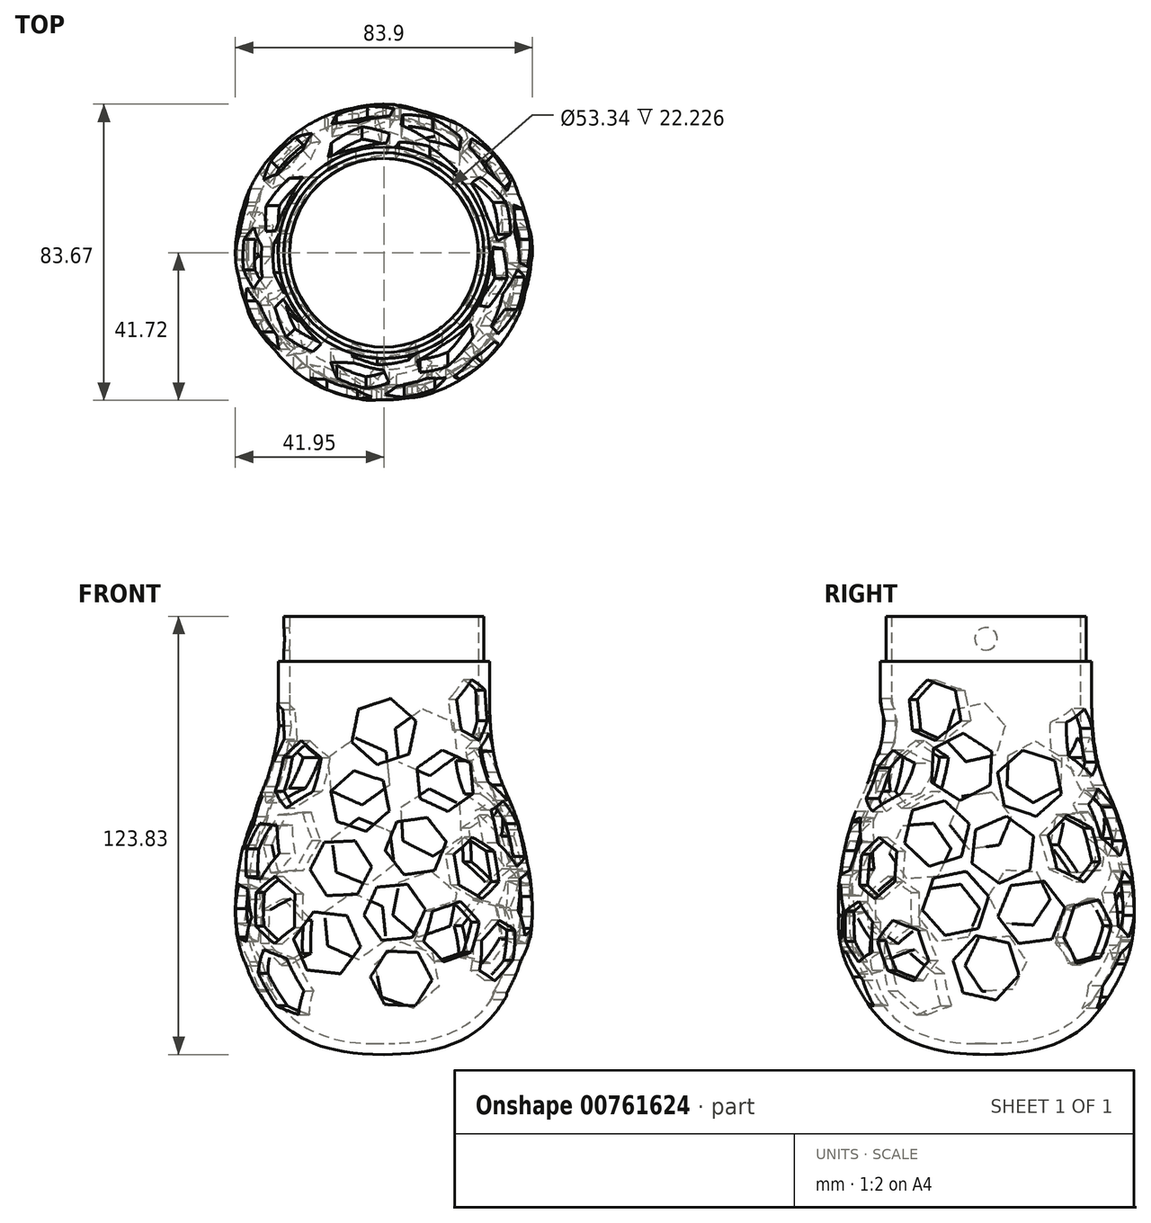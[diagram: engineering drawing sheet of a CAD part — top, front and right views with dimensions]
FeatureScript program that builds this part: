
annotation { "Feature Type Name" : "Feature", "Feature Type Description" : "" }
export const myFeature = defineFeature(function(context is Context, id is Id, definition is map)
    precondition{}
    {
        {
            var Q0;
            Q0=qCreatedBy(makeId("Front.planeOp"),FACE);
            var sketch = newSketch(context, id + "F0", { "sketchPlane" : qUnion([Q0])});
            skLineSegment(sketch, "E0.left", {"start": v(-29.85, -28.58) * mm, "end": v(-29.85, -50.8) * mm});
            skLineSegment(sketch, "E1", {"start": v(0, -149.22) * mm, "end": v(0, -152.4) * mm});
            skFitSpline(sketch, "E2", {"points": [v(-29.85, -50.8) * mm, v(-36.24, -82.2) * mm, v(-41.22, -101.6) * mm, v(-40.98, -121.67) * mm, v(-34.22, -136.68) * mm, v(0, -152.4) * mm], "startDerivative": vector(-0.05, -263.37) * mm, "endDerivative": vector(273.36, 0) * mm});
            skPoint(sketch, "E3.orphan", {"position": v(0, 0) * mm});
            skFitSpline(sketch, "E4.0", {"points": [v(-26.67, -50.8) * mm, v(-26.67, -56.4) * mm, v(-27.08, -63.07) * mm, v(-28.2, -69.67) * mm, v(-29.29, -73.73) * mm, v(-30.52, -77.1) * mm, v(-31.58, -79.5) * mm, v(-32.39, -81.3) * mm, v(-32.97, -82.6) * mm, v(-33.52, -83.93) * mm, v(-34.05, -85.32) * mm, v(-34.57, -86.78) * mm, v(-35.23, -88.8) * mm, v(-36, -91.47) * mm, v(-36.8, -94.82) * mm, v(-37.5, -98.27) * mm, v(-38.06, -101.77) * mm, v(-38.61, -106.45) * mm, v(-38.84, -111.04) * mm, v(-38.68, -115.4) * mm, v(-38.41, -118) * mm, v(-38.09, -120) * mm, v(-37.69, -121.9) * mm, v(-37.05, -124.18) * mm, v(-36.06, -126.82) * mm, v(-35.05, -128.98) * mm, v(-34.12, -130.72) * mm, v(-33.38, -132.03) * mm, v(-32.58, -133.36) * mm, v(-31.86, -134.5) * mm, v(-31.27, -135.4) * mm, v(-30.66, -136.31) * mm, v(-29.88, -137.43) * mm, v(-28.89, -138.73) * mm, v(-27.46, -140.42) * mm, v(-25.43, -142.4) * mm, v(-22.42, -144.57) * mm, v(-18.61, -146.45) * mm, v(-12.18, -148.46) * mm, v(-5.5, -149.23) * mm, v(0, -149.23) * mm]});
            skLineSegment(sketch, "E4.1", {"start": v(-26.67, -28.58) * mm, "end": v(-26.67, -50.8) * mm});
            skLineSegment(sketch, "E5", {"start": v(-26.67, 0) * mm, "end": v(0, 0) * mm, "construction": true});
            skLineSegment(sketch, "E6", {"start": v(0, -149.22) * mm, "end": v(0, 0) * mm, "construction": true});
            skLineSegment(sketch, "E7", {"start": v(-26.67, -28.58) * mm, "end": v(-29.85, -28.58) * mm});
            skLineSegment(sketch, "E8", {"start": v(-26.67, -28.58) * mm, "end": v(-26.67, 0) * mm, "construction": true});
            skSolve(sketch);
        }
        {
            var Q0;
            Q0 = qSketchRegion(id + "F0", true);
            var Q1;
            Q1=sQuery(id+"F0.wireOp",EDGE,"E6");
            revolve(context, id + "F1", {"surfaceOperationType" : NewSurfaceOperationType.NEW, "entities" : qUnion([Q0]), "axis" : qUnion([Q1]), "revolveType" : RevolveType.FULL});
        }
        {
            var Q0;
            Q0=qCreatedBy(makeId("Right.planeOp"),FACE);
            var sketch = newSketch(context, id + "F2", { "sketchPlane" : qUnion([Q0])});
            skCircle(sketch, "E9.cCircle", {"center": v(-18.57, -94.91) * mm, "radius": 7.55 * mm, "construction": true});
            skLineSegment(sketch, "E9.0", {"start": v(-22.35, -102.76) * mm, "end": v(-27.26, -95.57) * mm});
            skLineSegment(sketch, "E9.1", {"start": v(-27.26, -95.57) * mm, "end": v(-23.48, -87.72) * mm});
            skLineSegment(sketch, "E9.2", {"start": v(-23.48, -87.72) * mm, "end": v(-14.8, -87.06) * mm});
            skLineSegment(sketch, "E9.3", {"start": v(-14.8, -87.06) * mm, "end": v(-9.89, -94.26) * mm});
            skLineSegment(sketch, "E9.4", {"start": v(-9.89, -94.26) * mm, "end": v(-13.66, -102.11) * mm});
            skLineSegment(sketch, "E9.5", {"start": v(-13.66, -102.11) * mm, "end": v(-22.35, -102.76) * mm});
            skCircle(sketch, "E10.cCircle", {"center": v(-10.38, -112.38) * mm, "radius": 7.55 * mm, "construction": true});
            skLineSegment(sketch, "E10.0", {"start": v(-13.65, -120.45) * mm, "end": v(-19.01, -113.59) * mm});
            skLineSegment(sketch, "E10.1", {"start": v(-19.01, -113.59) * mm, "end": v(-15.74, -105.51) * mm});
            skLineSegment(sketch, "E10.2", {"start": v(-15.74, -105.51) * mm, "end": v(-7.12, -104.3) * mm});
            skLineSegment(sketch, "E10.3", {"start": v(-7.12, -104.3) * mm, "end": v(-1.76, -111.17) * mm});
            skLineSegment(sketch, "E10.4", {"start": v(-1.76, -111.17) * mm, "end": v(-5.02, -119.25) * mm});
            skLineSegment(sketch, "E10.5", {"start": v(-5.02, -119.25) * mm, "end": v(-13.65, -120.45) * mm});
            skPoint(sketch, "E10.0.midPoint", {"position": v(-16.33, -117.02) * mm});
            skCircle(sketch, "E11.cCircle", {"center": v(-1.56, -86.32) * mm, "radius": 7.55 * mm, "construction": true});
            skLineSegment(sketch, "E11.0", {"start": v(-4.8, -94.4) * mm, "end": v(-10.19, -87.55) * mm});
            skLineSegment(sketch, "E11.1", {"start": v(-10.19, -87.55) * mm, "end": v(-6.94, -79.46) * mm});
            skLineSegment(sketch, "E11.2", {"start": v(-6.94, -79.46) * mm, "end": v(1.69, -78.24) * mm});
            skLineSegment(sketch, "E11.3", {"start": v(1.69, -78.24) * mm, "end": v(7.07, -85.1) * mm});
            skLineSegment(sketch, "E11.4", {"start": v(7.07, -85.1) * mm, "end": v(3.82, -93.18) * mm});
            skLineSegment(sketch, "E11.5", {"start": v(3.82, -93.18) * mm, "end": v(-4.8, -94.4) * mm});
            skPoint(sketch, "E11.0.midPoint", {"position": v(-7.5, -90.98) * mm});
            skCircle(sketch, "E12.cCircle", {"center": v(9.45, -108.03) * mm, "radius": 7.55 * mm, "construction": true});
            skLineSegment(sketch, "E12.0", {"start": v(4.64, -115.3) * mm, "end": v(0.76, -107.5) * mm});
            skLineSegment(sketch, "E12.1", {"start": v(0.76, -107.5) * mm, "end": v(5.57, -100.23) * mm});
            skLineSegment(sketch, "E12.2", {"start": v(5.57, -100.23) * mm, "end": v(14.26, -100.77) * mm});
            skLineSegment(sketch, "E12.3", {"start": v(14.26, -100.77) * mm, "end": v(18.15, -108.57) * mm});
            skLineSegment(sketch, "E12.4", {"start": v(18.15, -108.57) * mm, "end": v(13.34, -115.83) * mm});
            skLineSegment(sketch, "E12.5", {"start": v(13.34, -115.83) * mm, "end": v(4.64, -115.3) * mm});
            skPoint(sketch, "E12.0.midPoint", {"position": v(2.7, -111.4) * mm});
            skCircle(sketch, "E13.cCircle", {"center": v(13.67, -72.51) * mm, "radius": 7.55 * mm, "construction": true});
            skLineSegment(sketch, "E13.0", {"start": v(13.34, -81.22) * mm, "end": v(5.97, -76.58) * mm});
            skLineSegment(sketch, "E13.1", {"start": v(5.97, -76.58) * mm, "end": v(6.3, -67.88) * mm});
            skLineSegment(sketch, "E13.2", {"start": v(6.3, -67.88) * mm, "end": v(14, -63.8) * mm});
            skLineSegment(sketch, "E13.3", {"start": v(14, -63.8) * mm, "end": v(21.37, -68.44) * mm});
            skLineSegment(sketch, "E13.4", {"start": v(21.37, -68.44) * mm, "end": v(21.04, -77.15) * mm});
            skLineSegment(sketch, "E13.5", {"start": v(21.04, -77.15) * mm, "end": v(13.34, -81.22) * mm});
            skPoint(sketch, "E13.0.midPoint", {"position": v(9.65, -78.9) * mm});
            skCircle(sketch, "E14.cCircle", {"center": v(-3.06, -61.34) * mm, "radius": 7.55 * mm, "construction": true});
            skLineSegment(sketch, "E14.0", {"start": v(-5.67, -69.66) * mm, "end": v(-11.56, -63.24) * mm});
            skLineSegment(sketch, "E14.1", {"start": v(-11.56, -63.24) * mm, "end": v(-8.96, -54.93) * mm});
            skLineSegment(sketch, "E14.2", {"start": v(-8.96, -54.93) * mm, "end": v(-0.45, -53.03) * mm});
            skLineSegment(sketch, "E14.3", {"start": v(-0.45, -53.03) * mm, "end": v(5.44, -59.44) * mm});
            skLineSegment(sketch, "E14.4", {"start": v(5.44, -59.44) * mm, "end": v(2.84, -67.76) * mm});
            skLineSegment(sketch, "E14.5", {"start": v(2.84, -67.76) * mm, "end": v(-5.67, -69.66) * mm});
            skPoint(sketch, "E14.0.midPoint", {"position": v(-8.61, -66.45) * mm});
            skCircle(sketch, "E15.cCircle", {"center": v(2.78, -126.74) * mm, "radius": 7.55 * mm, "construction": true});
            skLineSegment(sketch, "E15.0", {"start": v(-1.06, -134.56) * mm, "end": v(-5.91, -127.32) * mm});
            skLineSegment(sketch, "E15.1", {"start": v(-5.91, -127.32) * mm, "end": v(-2.07, -119.5) * mm});
            skLineSegment(sketch, "E15.2", {"start": v(-2.07, -119.5) * mm, "end": v(6.62, -118.92) * mm});
            skLineSegment(sketch, "E15.3", {"start": v(6.62, -118.92) * mm, "end": v(11.47, -126.15) * mm});
            skLineSegment(sketch, "E15.4", {"start": v(11.47, -126.15) * mm, "end": v(7.63, -133.97) * mm});
            skLineSegment(sketch, "E15.5", {"start": v(7.63, -133.97) * mm, "end": v(-1.06, -134.56) * mm});
            skPoint(sketch, "E15.0.midPoint", {"position": v(-3.48, -130.94) * mm});
            skSolve(sketch);
        }
        {
            var Q0;
            Q0 = qSketchRegion(id + "F2", true);
            var Q1;
            Q1=makeQuery(id+"F1.opRevolve","SWEPT_FACE",FACE,{"disambiguationData":[OSD([sQuery(id+"F0.wireOp",EDGE,"E4.0")])]});
            extrude(context, id + "F3", {"entities" : qUnion([Q0]), "operationType" : NewBodyOperationType.REMOVE, "endBound" : BoundingType.THROUGH_ALL, "oppositeDirection" : true, "depth" : 25.4 * mm, "endBoundEntityFace" : qUnion([Q1]), "offsetDistance" : 25.4 * mm});
        }
        {
            var Q0;
            Q0=qCreatedBy(makeId("Front.planeOp"),FACE);
            var sketch = newSketch(context, id + "F4", { "sketchPlane" : qUnion([Q0])});
            skCircle(sketch, "E16.cCircle", {"center": v(-7.1, -72.4) * mm, "radius": 8.26 * mm, "construction": true});
            skLineSegment(sketch, "E16.0", {"start": v(-8.02, -62.9) * mm, "end": v(0.66, -66.85) * mm});
            skLineSegment(sketch, "E16.1", {"start": v(0.66, -66.85) * mm, "end": v(1.58, -76.34) * mm});
            skLineSegment(sketch, "E16.2", {"start": v(1.58, -76.34) * mm, "end": v(-6.18, -81.88) * mm});
            skLineSegment(sketch, "E16.3", {"start": v(-6.18, -81.88) * mm, "end": v(-14.86, -77.94) * mm});
            skLineSegment(sketch, "E16.4", {"start": v(-14.86, -77.94) * mm, "end": v(-15.78, -68.45) * mm});
            skLineSegment(sketch, "E16.5", {"start": v(-15.78, -68.45) * mm, "end": v(-8.02, -62.9) * mm});
            skPoint(sketch, "E16.0.midPoint", {"position": v(-3.68, -64.88) * mm});
            skCircle(sketch, "E17.cCircle", {"center": v(11.95, -64.17) * mm, "radius": 8.26 * mm, "construction": true});
            skLineSegment(sketch, "E17.0", {"start": v(10.94, -54.7) * mm, "end": v(19.66, -58.56) * mm});
            skLineSegment(sketch, "E17.1", {"start": v(19.66, -58.56) * mm, "end": v(20.67, -68.04) * mm});
            skLineSegment(sketch, "E17.2", {"start": v(20.67, -68.04) * mm, "end": v(12.96, -73.65) * mm});
            skLineSegment(sketch, "E17.3", {"start": v(12.96, -73.65) * mm, "end": v(4.25, -69.79) * mm});
            skLineSegment(sketch, "E17.4", {"start": v(4.25, -69.79) * mm, "end": v(3.24, -60.3) * mm});
            skLineSegment(sketch, "E17.5", {"start": v(3.24, -60.3) * mm, "end": v(10.94, -54.7) * mm});
            skPoint(sketch, "E17.0.midPoint", {"position": v(15.3, -56.63) * mm});
            skCircle(sketch, "E18.cCircle", {"center": v(-5.9, -95.06) * mm, "radius": 8.26 * mm, "construction": true});
            skLineSegment(sketch, "E18.0", {"start": v(-7.14, -85.6) * mm, "end": v(1.67, -89.25) * mm});
            skLineSegment(sketch, "E18.1", {"start": v(1.67, -89.25) * mm, "end": v(2.91, -98.7) * mm});
            skLineSegment(sketch, "E18.2", {"start": v(2.91, -98.7) * mm, "end": v(-4.65, -104.5) * mm});
            skLineSegment(sketch, "E18.3", {"start": v(-4.65, -104.5) * mm, "end": v(-13.46, -100.86) * mm});
            skLineSegment(sketch, "E18.4", {"start": v(-13.46, -100.86) * mm, "end": v(-14.7, -91.4) * mm});
            skLineSegment(sketch, "E18.5", {"start": v(-14.7, -91.4) * mm, "end": v(-7.14, -85.6) * mm});
            skPoint(sketch, "E18.0.midPoint", {"position": v(-2.74, -87.43) * mm});
            skCircle(sketch, "E19.cCircle", {"center": v(-8.1, -116.11) * mm, "radius": 8.26 * mm, "construction": true});
            skLineSegment(sketch, "E19.0", {"start": v(-9.02, -106.62) * mm, "end": v(-0.34, -110.57) * mm});
            skLineSegment(sketch, "E19.1", {"start": v(-0.34, -110.57) * mm, "end": v(0.57, -120.06) * mm});
            skLineSegment(sketch, "E19.2", {"start": v(0.57, -120.06) * mm, "end": v(-7.19, -125.6) * mm});
            skLineSegment(sketch, "E19.3", {"start": v(-7.19, -125.6) * mm, "end": v(-15.86, -121.65) * mm});
            skLineSegment(sketch, "E19.4", {"start": v(-15.86, -121.65) * mm, "end": v(-16.78, -112.16) * mm});
            skLineSegment(sketch, "E19.5", {"start": v(-16.78, -112.16) * mm, "end": v(-9.02, -106.62) * mm});
            skPoint(sketch, "E19.0.midPoint", {"position": v(-4.68, -108.6) * mm});
            skCircle(sketch, "E20.cCircle", {"center": v(11.55, -109.9) * mm, "radius": 8.26 * mm, "construction": true});
            skLineSegment(sketch, "E20.0", {"start": v(13.32, -100.53) * mm, "end": v(20.55, -106.75) * mm});
            skLineSegment(sketch, "E20.1", {"start": v(20.55, -106.75) * mm, "end": v(18.78, -116.11) * mm});
            skLineSegment(sketch, "E20.2", {"start": v(18.78, -116.11) * mm, "end": v(9.78, -119.26) * mm});
            skLineSegment(sketch, "E20.3", {"start": v(9.78, -119.26) * mm, "end": v(2.55, -113.04) * mm});
            skLineSegment(sketch, "E20.4", {"start": v(2.55, -113.04) * mm, "end": v(4.33, -103.68) * mm});
            skLineSegment(sketch, "E20.5", {"start": v(4.33, -103.68) * mm, "end": v(13.32, -100.53) * mm});
            skPoint(sketch, "E20.0.midPoint", {"position": v(16.93, -103.64) * mm});
            skCircle(sketch, "E21.cCircle", {"center": v(13.36, -86.83) * mm, "radius": 8.26 * mm, "construction": true});
            skLineSegment(sketch, "E21.0", {"start": v(12.86, -77.31) * mm, "end": v(21.35, -81.65) * mm});
            skLineSegment(sketch, "E21.1", {"start": v(21.35, -81.65) * mm, "end": v(21.85, -91.17) * mm});
            skLineSegment(sketch, "E21.2", {"start": v(21.85, -91.17) * mm, "end": v(13.85, -96.35) * mm});
            skLineSegment(sketch, "E21.3", {"start": v(13.85, -96.35) * mm, "end": v(5.36, -92.02) * mm});
            skLineSegment(sketch, "E21.4", {"start": v(5.36, -92.02) * mm, "end": v(4.87, -82.5) * mm});
            skLineSegment(sketch, "E21.5", {"start": v(4.87, -82.5) * mm, "end": v(12.86, -77.31) * mm});
            skPoint(sketch, "E21.0.midPoint", {"position": v(17.1, -79.48) * mm});
            skCircle(sketch, "E22.cCircle", {"center": v(6.54, -129.95) * mm, "radius": 8.26 * mm, "construction": true});
            skLineSegment(sketch, "E22.0", {"start": v(4.73, -120.6) * mm, "end": v(13.74, -123.7) * mm});
            skLineSegment(sketch, "E22.1", {"start": v(13.74, -123.7) * mm, "end": v(15.55, -133.06) * mm});
            skLineSegment(sketch, "E22.2", {"start": v(15.55, -133.06) * mm, "end": v(8.34, -139.3) * mm});
            skLineSegment(sketch, "E22.3", {"start": v(8.34, -139.3) * mm, "end": v(-0.66, -136.2) * mm});
            skLineSegment(sketch, "E22.4", {"start": v(-0.66, -136.2) * mm, "end": v(-2.47, -126.83) * mm});
            skLineSegment(sketch, "E22.5", {"start": v(-2.47, -126.83) * mm, "end": v(4.73, -120.6) * mm});
            skPoint(sketch, "E22.0.midPoint", {"position": v(9.24, -122.15) * mm});
            skSolve(sketch);
        }
        {
            var Q0;
            Q0 = qSketchRegion(id + "F4", true);
            extrude(context, id + "F5", {"entities" : qUnion([Q0]), "operationType" : NewBodyOperationType.REMOVE, "endBound" : BoundingType.THROUGH_ALL, "oppositeDirection" : true, "depth" : 25.4 * mm, "offsetDistance" : 25.4 * mm});
        }
        {
            var Q0;
            Q0=qCreatedBy(makeId("Front.planeOp"),FACE);
            var sketch = newSketch(context, id + "F6", { "sketchPlane" : qUnion([Q0])});
            skCircle(sketch, "E23.cCircle", {"center": v(-12.14, -99.77) * mm, "radius": 7.55 * mm, "construction": true});
            skLineSegment(sketch, "E23.0", {"start": v(-16.14, -107.51) * mm, "end": v(-20.84, -100.18) * mm});
            skLineSegment(sketch, "E23.1", {"start": v(-20.84, -100.18) * mm, "end": v(-16.84, -92.44) * mm});
            skLineSegment(sketch, "E23.2", {"start": v(-16.84, -92.44) * mm, "end": v(-8.14, -92.03) * mm});
            skLineSegment(sketch, "E23.3", {"start": v(-8.14, -92.03) * mm, "end": v(-3.44, -99.37) * mm});
            skLineSegment(sketch, "E23.4", {"start": v(-3.44, -99.37) * mm, "end": v(-7.44, -107.1) * mm});
            skLineSegment(sketch, "E23.5", {"start": v(-7.44, -107.1) * mm, "end": v(-16.14, -107.51) * mm});
            skPoint(sketch, "E23.0.midPoint", {"position": v(-18.5, -103.84) * mm});
            skCircle(sketch, "E24.cCircle", {"center": v(3.05, -112.22) * mm, "radius": 7.55 * mm, "construction": true});
            skLineSegment(sketch, "E24.0", {"start": v(-0.59, -120.14) * mm, "end": v(-5.63, -113.03) * mm});
            skLineSegment(sketch, "E24.1", {"start": v(-5.63, -113.03) * mm, "end": v(-2, -105.11) * mm});
            skLineSegment(sketch, "E24.2", {"start": v(-2, -105.11) * mm, "end": v(6.68, -104.3) * mm});
            skLineSegment(sketch, "E24.3", {"start": v(6.68, -104.3) * mm, "end": v(11.72, -111.4) * mm});
            skLineSegment(sketch, "E24.4", {"start": v(11.72, -111.4) * mm, "end": v(8.09, -119.33) * mm});
            skLineSegment(sketch, "E24.5", {"start": v(8.09, -119.33) * mm, "end": v(-0.59, -120.14) * mm});
            skPoint(sketch, "E24.0.midPoint", {"position": v(-3.1, -116.58) * mm});
            skCircle(sketch, "E25.cCircle", {"center": v(9, -93.53) * mm, "radius": 7.55 * mm, "construction": true});
            skLineSegment(sketch, "E25.0", {"start": v(5.74, -101.61) * mm, "end": v(0.37, -94.76) * mm});
            skLineSegment(sketch, "E25.1", {"start": v(0.37, -94.76) * mm, "end": v(3.62, -86.67) * mm});
            skLineSegment(sketch, "E25.2", {"start": v(3.62, -86.67) * mm, "end": v(12.24, -85.44) * mm});
            skLineSegment(sketch, "E25.3", {"start": v(12.24, -85.44) * mm, "end": v(17.62, -92.3) * mm});
            skLineSegment(sketch, "E25.4", {"start": v(17.62, -92.3) * mm, "end": v(14.37, -100.38) * mm});
            skLineSegment(sketch, "E25.5", {"start": v(14.37, -100.38) * mm, "end": v(5.74, -101.61) * mm});
            skPoint(sketch, "E25.0.midPoint", {"position": v(3.06, -98.18) * mm});
            skCircle(sketch, "E26.cCircle", {"center": v(17.31, -75.04) * mm, "radius": 7.55 * mm, "construction": true});
            skLineSegment(sketch, "E26.0", {"start": v(18.1, -83.72) * mm, "end": v(10.2, -80.06) * mm});
            skLineSegment(sketch, "E26.1", {"start": v(10.2, -80.06) * mm, "end": v(9.4, -71.39) * mm});
            skLineSegment(sketch, "E26.2", {"start": v(9.4, -71.39) * mm, "end": v(16.52, -66.36) * mm});
            skLineSegment(sketch, "E26.3", {"start": v(16.52, -66.36) * mm, "end": v(24.43, -70.02) * mm});
            skLineSegment(sketch, "E26.4", {"start": v(24.43, -70.02) * mm, "end": v(25.22, -78.7) * mm});
            skLineSegment(sketch, "E26.5", {"start": v(25.22, -78.7) * mm, "end": v(18.1, -83.72) * mm});
            skPoint(sketch, "E26.0.midPoint", {"position": v(14.15, -81.9) * mm});
            skCircle(sketch, "E27.cCircle", {"center": v(-6.72, -80.77) * mm, "radius": 7.55 * mm, "construction": true});
            skLineSegment(sketch, "E27.0", {"start": v(-5.02, -89.32) * mm, "end": v(-13.27, -86.52) * mm});
            skLineSegment(sketch, "E27.1", {"start": v(-13.27, -86.52) * mm, "end": v(-14.97, -77.97) * mm});
            skLineSegment(sketch, "E27.2", {"start": v(-14.97, -77.97) * mm, "end": v(-8.42, -72.23) * mm});
            skLineSegment(sketch, "E27.3", {"start": v(-8.42, -72.23) * mm, "end": v(-0.17, -75.03) * mm});
            skLineSegment(sketch, "E27.4", {"start": v(-0.17, -75.03) * mm, "end": v(1.53, -83.57) * mm});
            skLineSegment(sketch, "E27.5", {"start": v(1.53, -83.57) * mm, "end": v(-5.02, -89.32) * mm});
            skPoint(sketch, "E27.0.midPoint", {"position": v(-9.14, -87.92) * mm});
            skCircle(sketch, "E28.cCircle", {"center": v(4.92, -130.9) * mm, "radius": 7.55 * mm, "construction": true});
            skLineSegment(sketch, "E28.0", {"start": v(0.22, -138.24) * mm, "end": v(-3.79, -130.5) * mm});
            skLineSegment(sketch, "E28.1", {"start": v(-3.79, -130.5) * mm, "end": v(0.91, -123.17) * mm});
            skLineSegment(sketch, "E28.2", {"start": v(0.91, -123.17) * mm, "end": v(9.62, -123.57) * mm});
            skLineSegment(sketch, "E28.3", {"start": v(9.62, -123.57) * mm, "end": v(13.62, -131.3) * mm});
            skLineSegment(sketch, "E28.4", {"start": v(13.62, -131.3) * mm, "end": v(8.92, -138.65) * mm});
            skLineSegment(sketch, "E28.5", {"start": v(8.92, -138.65) * mm, "end": v(0.22, -138.24) * mm});
            skPoint(sketch, "E28.0.midPoint", {"position": v(-1.78, -134.37) * mm});
            skCircle(sketch, "E29.cCircle", {"center": v(-16.05, -120.85) * mm, "radius": 8.26 * mm, "construction": true});
            skLineSegment(sketch, "E29.0", {"start": v(-21.7, -128.52) * mm, "end": v(-25.52, -119.78) * mm});
            skLineSegment(sketch, "E29.1", {"start": v(-25.52, -119.78) * mm, "end": v(-19.86, -112.11) * mm});
            skLineSegment(sketch, "E29.2", {"start": v(-19.86, -112.11) * mm, "end": v(-10.4, -113.18) * mm});
            skLineSegment(sketch, "E29.3", {"start": v(-10.4, -113.18) * mm, "end": v(-6.58, -121.91) * mm});
            skLineSegment(sketch, "E29.4", {"start": v(-6.58, -121.91) * mm, "end": v(-12.23, -129.58) * mm});
            skLineSegment(sketch, "E29.5", {"start": v(-12.23, -129.58) * mm, "end": v(-21.7, -128.52) * mm});
            skPoint(sketch, "E29.0.midPoint", {"position": v(-23.61, -124.15) * mm});
            skCircle(sketch, "E30.cCircle", {"center": v(0, -61.14) * mm, "radius": 8.26 * mm, "construction": true});
            skLineSegment(sketch, "E30.0", {"start": v(7.14, -67.45) * mm, "end": v(-1.9, -70.48) * mm});
            skLineSegment(sketch, "E30.1", {"start": v(-1.9, -70.48) * mm, "end": v(-9.04, -64.16) * mm});
            skLineSegment(sketch, "E30.2", {"start": v(-9.04, -64.16) * mm, "end": v(-7.14, -54.82) * mm});
            skLineSegment(sketch, "E30.3", {"start": v(-7.14, -54.82) * mm, "end": v(1.9, -51.8) * mm});
            skLineSegment(sketch, "E30.4", {"start": v(1.9, -51.8) * mm, "end": v(9.04, -58.11) * mm});
            skLineSegment(sketch, "E30.5", {"start": v(9.04, -58.11) * mm, "end": v(7.14, -67.45) * mm});
            skPoint(sketch, "E30.0.midPoint", {"position": v(2.62, -68.97) * mm});
            skSolve(sketch);
        }
        {
            var Q0;
            Q0 = qSketchRegion(id + "F6", true);
            extrude(context, id + "F7", {"entities" : qUnion([Q0]), "operationType" : NewBodyOperationType.REMOVE, "endBound" : BoundingType.THROUGH_ALL, "depth" : 25.4 * mm, "offsetDistance" : 25.4 * mm});
        }
        {
            var Q0;
            Q0=qCreatedBy(makeId("Right.planeOp"),FACE);
            var sketch = newSketch(context, id + "F8", { "sketchPlane" : qUnion([Q0])});
            skCircle(sketch, "E31.cCircle", {"center": v(-8.55, -109.7) * mm, "radius": 8.26 * mm, "construction": true});
            skLineSegment(sketch, "E31.0", {"start": v(-11.55, -118.74) * mm, "end": v(-17.89, -111.62) * mm});
            skLineSegment(sketch, "E31.1", {"start": v(-17.89, -111.62) * mm, "end": v(-14.89, -102.57) * mm});
            skLineSegment(sketch, "E31.2", {"start": v(-14.89, -102.57) * mm, "end": v(-5.55, -100.65) * mm});
            skLineSegment(sketch, "E31.3", {"start": v(-5.55, -100.65) * mm, "end": v(0.78, -107.77) * mm});
            skLineSegment(sketch, "E31.4", {"start": v(0.78, -107.77) * mm, "end": v(-2.22, -116.82) * mm});
            skLineSegment(sketch, "E31.5", {"start": v(-2.22, -116.82) * mm, "end": v(-11.55, -118.74) * mm});
            skPoint(sketch, "E31.0.midPoint", {"position": v(-14.72, -115.18) * mm});
            skCircle(sketch, "E32.cCircle", {"center": v(4.75, -94.53) * mm, "radius": 8.26 * mm, "construction": true});
            skLineSegment(sketch, "E32.0", {"start": v(3.73, -104.01) * mm, "end": v(-3.97, -98.39) * mm});
            skLineSegment(sketch, "E32.1", {"start": v(-3.97, -98.39) * mm, "end": v(-2.94, -88.9) * mm});
            skLineSegment(sketch, "E32.2", {"start": v(-2.94, -88.9) * mm, "end": v(5.78, -85.06) * mm});
            skLineSegment(sketch, "E32.3", {"start": v(5.78, -85.06) * mm, "end": v(13.47, -90.68) * mm});
            skLineSegment(sketch, "E32.4", {"start": v(13.47, -90.68) * mm, "end": v(12.45, -100.16) * mm});
            skLineSegment(sketch, "E32.5", {"start": v(12.45, -100.16) * mm, "end": v(3.73, -104.01) * mm});
            skPoint(sketch, "E32.0.midPoint", {"position": v(-0.12, -101.2) * mm});
            skCircle(sketch, "E33.cCircle", {"center": v(12.86, -112.22) * mm, "radius": 8.26 * mm, "construction": true});
            skLineSegment(sketch, "E33.0", {"start": v(9.2, -121.03) * mm, "end": v(3.4, -113.46) * mm});
            skLineSegment(sketch, "E33.1", {"start": v(3.4, -113.46) * mm, "end": v(7.06, -104.66) * mm});
            skLineSegment(sketch, "E33.2", {"start": v(7.06, -104.66) * mm, "end": v(16.5, -103.42) * mm});
            skLineSegment(sketch, "E33.3", {"start": v(16.5, -103.42) * mm, "end": v(22.3, -110.98) * mm});
            skLineSegment(sketch, "E33.4", {"start": v(22.3, -110.98) * mm, "end": v(18.66, -119.78) * mm});
            skLineSegment(sketch, "E33.5", {"start": v(18.66, -119.78) * mm, "end": v(9.2, -121.03) * mm});
            skPoint(sketch, "E33.0.midPoint", {"position": v(6.3, -117.25) * mm});
            skCircle(sketch, "E34.cCircle", {"center": v(12.3, -75.74) * mm, "radius": 8.26 * mm, "construction": true});
            skLineSegment(sketch, "E34.0", {"start": v(14.2, -85.09) * mm, "end": v(5.16, -82.05) * mm});
            skLineSegment(sketch, "E34.1", {"start": v(5.16, -82.05) * mm, "end": v(3.27, -72.7) * mm});
            skLineSegment(sketch, "E34.2", {"start": v(3.27, -72.7) * mm, "end": v(10.42, -66.4) * mm});
            skLineSegment(sketch, "E34.3", {"start": v(10.42, -66.4) * mm, "end": v(19.45, -69.44) * mm});
            skLineSegment(sketch, "E34.4", {"start": v(19.45, -69.44) * mm, "end": v(21.34, -78.78) * mm});
            skLineSegment(sketch, "E34.5", {"start": v(21.34, -78.78) * mm, "end": v(14.2, -85.09) * mm});
            skPoint(sketch, "E34.0.midPoint", {"position": v(9.68, -83.57) * mm});
            skCircle(sketch, "E35.cCircle", {"center": v(-6.85, -71.14) * mm, "radius": 8.26 * mm, "construction": true});
            skLineSegment(sketch, "E35.0", {"start": v(-7.32, -80.66) * mm, "end": v(-15.33, -75.5) * mm});
            skLineSegment(sketch, "E35.1", {"start": v(-15.33, -75.5) * mm, "end": v(-14.87, -65.97) * mm});
            skLineSegment(sketch, "E35.2", {"start": v(-14.87, -65.97) * mm, "end": v(-6.39, -61.62) * mm});
            skLineSegment(sketch, "E35.3", {"start": v(-6.39, -61.62) * mm, "end": v(1.62, -66.78) * mm});
            skLineSegment(sketch, "E35.4", {"start": v(1.62, -66.78) * mm, "end": v(1.16, -76.3) * mm});
            skLineSegment(sketch, "E35.5", {"start": v(1.16, -76.3) * mm, "end": v(-7.32, -80.66) * mm});
            skPoint(sketch, "E35.0.midPoint", {"position": v(-11.33, -78.08) * mm});
            skCircle(sketch, "E36.cCircle", {"center": v(0, -127.91) * mm, "radius": 8.26 * mm, "construction": true});
            skLineSegment(sketch, "E36.0", {"start": v(-6.45, -134.93) * mm, "end": v(-9.3, -125.84) * mm});
            skLineSegment(sketch, "E36.1", {"start": v(-9.3, -125.84) * mm, "end": v(-2.86, -118.82) * mm});
            skLineSegment(sketch, "E36.2", {"start": v(-2.86, -118.82) * mm, "end": v(6.45, -120.9) * mm});
            skLineSegment(sketch, "E36.3", {"start": v(6.45, -120.9) * mm, "end": v(9.3, -129.99) * mm});
            skLineSegment(sketch, "E36.4", {"start": v(9.3, -129.99) * mm, "end": v(2.86, -137) * mm});
            skLineSegment(sketch, "E36.5", {"start": v(2.86, -137) * mm, "end": v(-6.45, -134.93) * mm});
            skPoint(sketch, "E36.0.midPoint", {"position": v(-7.88, -130.39) * mm});
            skCircle(sketch, "E37.cCircle", {"center": v(-13.86, -89.93) * mm, "radius": 8.26 * mm, "construction": true});
            skLineSegment(sketch, "E37.0", {"start": v(-16.05, -99.2) * mm, "end": v(-22.99, -92.67) * mm});
            skLineSegment(sketch, "E37.1", {"start": v(-22.99, -92.67) * mm, "end": v(-20.8, -83.4) * mm});
            skLineSegment(sketch, "E37.2", {"start": v(-20.8, -83.4) * mm, "end": v(-11.67, -80.65) * mm});
            skLineSegment(sketch, "E37.3", {"start": v(-11.67, -80.65) * mm, "end": v(-4.73, -87.19) * mm});
            skLineSegment(sketch, "E37.4", {"start": v(-4.73, -87.19) * mm, "end": v(-6.92, -96.46) * mm});
            skLineSegment(sketch, "E37.5", {"start": v(-6.92, -96.46) * mm, "end": v(-16.05, -99.2) * mm});
            skSolve(sketch);
        }
        {
            var Q0;
            Q0 = qSketchRegion(id + "F8", true);
            extrude(context, id + "F9", {"entities" : qUnion([Q0]), "operationType" : NewBodyOperationType.REMOVE, "endBound" : BoundingType.THROUGH_ALL, "depth" : 25.4 * mm, "offsetDistance" : 25.4 * mm});
        }
        {
            var Q0;
            Q0=qCreatedBy(makeId("Right.planeOp"),FACE);
            var Q1;
            Q1=qCreatedBy(makeId("Front.planeOp"),FACE);
            cPlane(context, id + "F10", {"entities" : qUnion([Q0, Q1]), "cplaneType" : CPlaneType.MID_PLANE, "offset" : 25.4 * mm, "flipAlignment" : true, "width" : 152.4 * mm, "height" : 152.4 * mm});
        }
        {
            var Q0;
            Q0=qCreatedBy(makeId("Front.planeOp"),FACE);
            var Q1;
            Q1=qCreatedBy(makeId("Right.planeOp"),FACE);
            cPlane(context, id + "F11", {"entities" : qUnion([Q0, Q1]), "cplaneType" : CPlaneType.MID_PLANE, "offset" : 25.4 * mm, "width" : 152.4 * mm, "height" : 152.4 * mm});
        }
        {
            var Q0;
            Q0=qCreatedBy(id+"F11.planeOp",FACE);
            var sketch = newSketch(context, id + "F12", { "sketchPlane" : qUnion([Q0])});
            skCircle(sketch, "E38.cCircle", {"center": v(0, -117.65) * mm, "radius": 8.26 * mm, "construction": true});
            skLineSegment(sketch, "E38.0", {"start": v(-9.39, -115.98) * mm, "end": v(-3.25, -108.69) * mm});
            skLineSegment(sketch, "E38.1", {"start": v(-3.25, -108.69) * mm, "end": v(6.14, -110.35) * mm});
            skLineSegment(sketch, "E38.2", {"start": v(6.14, -110.35) * mm, "end": v(9.39, -119.32) * mm});
            skLineSegment(sketch, "E38.3", {"start": v(9.39, -119.32) * mm, "end": v(3.25, -126.61) * mm});
            skLineSegment(sketch, "E38.4", {"start": v(3.25, -126.61) * mm, "end": v(-6.14, -124.94) * mm});
            skLineSegment(sketch, "E38.5", {"start": v(-6.14, -124.94) * mm, "end": v(-9.39, -115.98) * mm});
            skPoint(sketch, "E38.0.midPoint", {"position": v(-6.32, -112.34) * mm});
            skCircle(sketch, "E39.cCircle", {"center": v(3.47, -94.2) * mm, "radius": 8.25 * mm, "construction": true});
            skLineSegment(sketch, "E39.0", {"start": v(2.3, -103.66) * mm, "end": v(-5.3, -97.92) * mm});
            skLineSegment(sketch, "E39.1", {"start": v(-5.3, -97.92) * mm, "end": v(-4.14, -88.46) * mm});
            skLineSegment(sketch, "E39.2", {"start": v(-4.14, -88.46) * mm, "end": v(4.64, -84.74) * mm});
            skLineSegment(sketch, "E39.3", {"start": v(4.64, -84.74) * mm, "end": v(12.25, -90.48) * mm});
            skLineSegment(sketch, "E39.4", {"start": v(12.25, -90.48) * mm, "end": v(11.08, -99.94) * mm});
            skLineSegment(sketch, "E39.5", {"start": v(11.08, -99.94) * mm, "end": v(2.3, -103.66) * mm});
            skPoint(sketch, "E39.0.midPoint", {"position": v(-1.5, -100.8) * mm});
            skCircle(sketch, "E40.cCircle", {"center": v(-97.25, -84.42) * mm, "radius": 8.26 * mm, "construction": true});
            skLineSegment(sketch, "E40.0", {"start": v(-106, -88.23) * mm, "end": v(-104.92, -78.76) * mm});
            skLineSegment(sketch, "E40.1", {"start": v(-104.92, -78.76) * mm, "end": v(-96.18, -74.95) * mm});
            skLineSegment(sketch, "E40.2", {"start": v(-96.18, -74.95) * mm, "end": v(-88.51, -80.61) * mm});
            skLineSegment(sketch, "E40.3", {"start": v(-88.51, -80.61) * mm, "end": v(-89.59, -90.08) * mm});
            skLineSegment(sketch, "E40.4", {"start": v(-89.59, -90.08) * mm, "end": v(-98.32, -93.9) * mm});
            skLineSegment(sketch, "E40.5", {"start": v(-98.32, -93.9) * mm, "end": v(-106, -88.23) * mm});
            skPoint(sketch, "E40.0.midPoint", {"position": v(-105.46, -83.5) * mm});
            skSolve(sketch);
        }
        {
            var Q0;
            Q0 = qSketchRegion(id + "F12", true);
            extrude(context, id + "F13", {"entities" : qUnion([Q0]), "operationType" : NewBodyOperationType.REMOVE, "endBound" : BoundingType.THROUGH_ALL, "oppositeDirection" : true, "depth" : 25.4 * mm, "offsetDistance" : 25.4 * mm});
        }
        {
            var Q0;
            Q0=qCreatedBy(id+"F10.planeOp",FACE);
            var sketch = newSketch(context, id + "F14", { "sketchPlane" : qUnion([Q0])});
            skCircle(sketch, "E41.cCircle", {"center": v(0, -92.5) * mm, "radius": 8.26 * mm, "construction": true});
            skLineSegment(sketch, "E41.0", {"start": v(-4.18, -101.06) * mm, "end": v(-9.5, -93.16) * mm});
            skLineSegment(sketch, "E41.1", {"start": v(-9.5, -93.16) * mm, "end": v(-5.33, -84.6) * mm});
            skLineSegment(sketch, "E41.2", {"start": v(-5.33, -84.6) * mm, "end": v(4.18, -83.93) * mm});
            skLineSegment(sketch, "E41.3", {"start": v(4.18, -83.93) * mm, "end": v(9.5, -91.83) * mm});
            skLineSegment(sketch, "E41.4", {"start": v(9.5, -91.83) * mm, "end": v(5.33, -100.4) * mm});
            skLineSegment(sketch, "E41.5", {"start": v(5.33, -100.4) * mm, "end": v(-4.18, -101.06) * mm});
            skPoint(sketch, "E41.0.midPoint", {"position": v(-6.84, -97.11) * mm});
            skCircle(sketch, "E42.cCircle", {"center": v(0, -117.74) * mm, "radius": 8.26 * mm, "construction": true});
            skLineSegment(sketch, "E42.0", {"start": v(-1.66, -127.12) * mm, "end": v(-8.96, -121) * mm});
            skLineSegment(sketch, "E42.1", {"start": v(-8.96, -121) * mm, "end": v(-7.3, -111.6) * mm});
            skLineSegment(sketch, "E42.2", {"start": v(-7.3, -111.6) * mm, "end": v(1.66, -108.35) * mm});
            skLineSegment(sketch, "E42.3", {"start": v(1.66, -108.35) * mm, "end": v(8.96, -114.48) * mm});
            skLineSegment(sketch, "E42.4", {"start": v(8.96, -114.48) * mm, "end": v(7.3, -123.87) * mm});
            skLineSegment(sketch, "E42.5", {"start": v(7.3, -123.87) * mm, "end": v(-1.66, -127.12) * mm});
            skPoint(sketch, "E42.0.midPoint", {"position": v(-5.3, -124.06) * mm});
            skCircle(sketch, "E43.cCircle", {"center": v(-75.64, -139.93) * mm, "radius": 8.26 * mm, "construction": true});
            skLineSegment(sketch, "E43.0", {"start": v(-84.55, -143.32) * mm, "end": v(-83.03, -133.91) * mm});
            skLineSegment(sketch, "E43.1", {"start": v(-83.03, -133.91) * mm, "end": v(-74.12, -130.52) * mm});
            skLineSegment(sketch, "E43.2", {"start": v(-74.12, -130.52) * mm, "end": v(-66.73, -136.55) * mm});
            skLineSegment(sketch, "E43.3", {"start": v(-66.73, -136.55) * mm, "end": v(-68.25, -145.96) * mm});
            skLineSegment(sketch, "E43.4", {"start": v(-68.25, -145.96) * mm, "end": v(-77.16, -149.34) * mm});
            skLineSegment(sketch, "E43.5", {"start": v(-77.16, -149.34) * mm, "end": v(-84.55, -143.32) * mm});
            skPoint(sketch, "E43.0.midPoint", {"position": v(-83.79, -138.62) * mm});
            skSolve(sketch);
        }
        {
            var Q0;
            Q0 = qSketchRegion(id + "F14", true);
            extrude(context, id + "F15", {"entities" : qUnion([Q0]), "operationType" : NewBodyOperationType.REMOVE, "endBound" : BoundingType.THROUGH_ALL, "oppositeDirection" : true, "depth" : 25.4 * mm, "offsetDistance" : 25.4 * mm});
        }
        {
            var Q0;
            Q0=qCreatedBy(id+"F11.planeOp",FACE);
            var sketch = newSketch(context, id + "F16", { "sketchPlane" : qUnion([Q0])});
            skCircle(sketch, "E44.cCircle", {"center": v(-2.44, -111.53) * mm, "radius": 8.26 * mm, "construction": true});
            skLineSegment(sketch, "E44.0", {"start": v(-2.65, -121.06) * mm, "end": v(-10.8, -116.12) * mm});
            skLineSegment(sketch, "E44.1", {"start": v(-10.8, -116.12) * mm, "end": v(-10.6, -106.6) * mm});
            skLineSegment(sketch, "E44.2", {"start": v(-10.6, -106.6) * mm, "end": v(-2.24, -102) * mm});
            skLineSegment(sketch, "E44.3", {"start": v(-2.24, -102) * mm, "end": v(5.91, -106.95) * mm});
            skLineSegment(sketch, "E44.4", {"start": v(5.91, -106.95) * mm, "end": v(5.7, -116.48) * mm});
            skLineSegment(sketch, "E44.5", {"start": v(5.7, -116.48) * mm, "end": v(-2.65, -121.06) * mm});
            skPoint(sketch, "E44.0.midPoint", {"position": v(-6.72, -118.6) * mm});
            skCircle(sketch, "E45.cCircle", {"center": v(-2.56, -73.26) * mm, "radius": 8.26 * mm, "construction": true});
            skLineSegment(sketch, "E45.0", {"start": v(-10.78, -68.43) * mm, "end": v(-2.5, -63.73) * mm});
            skLineSegment(sketch, "E45.1", {"start": v(-2.5, -63.73) * mm, "end": v(5.73, -68.55) * mm});
            skLineSegment(sketch, "E45.2", {"start": v(5.73, -68.55) * mm, "end": v(5.66, -78.08) * mm});
            skLineSegment(sketch, "E45.3", {"start": v(5.66, -78.08) * mm, "end": v(-2.63, -82.79) * mm});
            skLineSegment(sketch, "E45.4", {"start": v(-2.63, -82.79) * mm, "end": v(-10.85, -77.96) * mm});
            skLineSegment(sketch, "E45.5", {"start": v(-10.85, -77.96) * mm, "end": v(-10.78, -68.43) * mm});
            skPoint(sketch, "E45.0.midPoint", {"position": v(-6.64, -66.08) * mm});
            skCircle(sketch, "E46.cCircle", {"center": v(-5.66, -131.93) * mm, "radius": 8.26 * mm, "construction": true});
            skLineSegment(sketch, "E46.0", {"start": v(-12.43, -138.64) * mm, "end": v(-14.86, -129.42) * mm});
            skLineSegment(sketch, "E46.1", {"start": v(-14.86, -129.42) * mm, "end": v(-8.1, -122.7) * mm});
            skLineSegment(sketch, "E46.2", {"start": v(-8.1, -122.7) * mm, "end": v(1.1, -125.21) * mm});
            skLineSegment(sketch, "E46.3", {"start": v(1.1, -125.21) * mm, "end": v(3.53, -134.43) * mm});
            skLineSegment(sketch, "E46.4", {"start": v(3.53, -134.43) * mm, "end": v(-3.23, -141.14) * mm});
            skLineSegment(sketch, "E46.5", {"start": v(-3.23, -141.14) * mm, "end": v(-12.43, -138.64) * mm});
            skPoint(sketch, "E46.0.midPoint", {"position": v(-13.64, -134.03) * mm});
            skSolve(sketch);
        }
        {
            var Q0;
            Q0 = qSketchRegion(id + "F16", true);
            extrude(context, id + "F17", {"entities" : qUnion([Q0]), "operationType" : NewBodyOperationType.REMOVE, "endBound" : BoundingType.THROUGH_ALL, "depth" : 25.4 * mm, "offsetDistance" : 25.4 * mm});
        }
        {
            var Q0;
            Q0=qCreatedBy(id+"F10.planeOp",FACE);
            var sketch = newSketch(context, id + "F18", { "sketchPlane" : qUnion([Q0])});
            skCircle(sketch, "E47.cCircle", {"center": v(-11.83, -117.68) * mm, "radius": 7.55 * mm, "construction": true});
            skLineSegment(sketch, "E47.0", {"start": v(-13.58, -126.21) * mm, "end": v(-20.1, -120.44) * mm});
            skLineSegment(sketch, "E47.1", {"start": v(-20.1, -120.44) * mm, "end": v(-18.35, -111.9) * mm});
            skLineSegment(sketch, "E47.2", {"start": v(-18.35, -111.9) * mm, "end": v(-10.09, -109.14) * mm});
            skLineSegment(sketch, "E47.3", {"start": v(-10.09, -109.14) * mm, "end": v(-3.57, -114.92) * mm});
            skLineSegment(sketch, "E47.4", {"start": v(-3.57, -114.92) * mm, "end": v(-5.31, -123.46) * mm});
            skLineSegment(sketch, "E47.5", {"start": v(-5.31, -123.46) * mm, "end": v(-13.58, -126.21) * mm});
            skPoint(sketch, "E47.0.midPoint", {"position": v(-16.84, -123.33) * mm});
            skCircle(sketch, "E48.cCircle", {"center": v(7.42, -55.1) * mm, "radius": 7.55 * mm, "construction": true});
            skLineSegment(sketch, "E48.0", {"start": v(8.96, -63.68) * mm, "end": v(0.76, -60.73) * mm});
            skLineSegment(sketch, "E48.1", {"start": v(0.76, -60.73) * mm, "end": v(-0.78, -52.15) * mm});
            skLineSegment(sketch, "E48.2", {"start": v(-0.78, -52.15) * mm, "end": v(5.88, -46.53) * mm});
            skLineSegment(sketch, "E48.3", {"start": v(5.88, -46.53) * mm, "end": v(14.08, -49.49) * mm});
            skLineSegment(sketch, "E48.4", {"start": v(14.08, -49.49) * mm, "end": v(15.61, -58.07) * mm});
            skLineSegment(sketch, "E48.5", {"start": v(15.61, -58.07) * mm, "end": v(8.96, -63.68) * mm});
            skPoint(sketch, "E48.0.midPoint", {"position": v(4.86, -62.2) * mm});
            skCircle(sketch, "E49.cCircle", {"center": v(6.13, -123) * mm, "radius": 7.55 * mm, "construction": true});
            skLineSegment(sketch, "E49.0", {"start": v(7.8, -131.55) * mm, "end": v(-0.45, -128.72) * mm});
            skLineSegment(sketch, "E49.1", {"start": v(-0.45, -128.72) * mm, "end": v(-2.11, -120.17) * mm});
            skLineSegment(sketch, "E49.2", {"start": v(-2.11, -120.17) * mm, "end": v(4.46, -114.45) * mm});
            skLineSegment(sketch, "E49.3", {"start": v(4.46, -114.45) * mm, "end": v(12.7, -117.29) * mm});
            skLineSegment(sketch, "E49.4", {"start": v(12.7, -117.29) * mm, "end": v(14.37, -125.84) * mm});
            skLineSegment(sketch, "E49.5", {"start": v(14.37, -125.84) * mm, "end": v(7.8, -131.55) * mm});
            skPoint(sketch, "E49.0.midPoint", {"position": v(3.67, -130.14) * mm});
            skCircle(sketch, "E50.cCircle", {"center": v(-3.01, -99.73) * mm, "radius": 7.55 * mm, "construction": true});
            skLineSegment(sketch, "E50.0", {"start": v(-10.27, -104.55) * mm, "end": v(-10.81, -95.85) * mm});
            skLineSegment(sketch, "E50.1", {"start": v(-10.81, -95.85) * mm, "end": v(-3.55, -91.03) * mm});
            skLineSegment(sketch, "E50.2", {"start": v(-3.55, -91.03) * mm, "end": v(4.25, -94.91) * mm});
            skLineSegment(sketch, "E50.3", {"start": v(4.25, -94.91) * mm, "end": v(4.8, -103.6) * mm});
            skLineSegment(sketch, "E50.4", {"start": v(4.8, -103.6) * mm, "end": v(-2.47, -108.42) * mm});
            skLineSegment(sketch, "E50.5", {"start": v(-2.47, -108.42) * mm, "end": v(-10.27, -104.55) * mm});
            skPoint(sketch, "E50.0.midPoint", {"position": v(-10.54, -100.2) * mm});
            skSolve(sketch);
        }
        {
            var Q0;
            Q0 = qSketchRegion(id + "F18", true);
            extrude(context, id + "F19", {"entities" : qUnion([Q0]), "operationType" : NewBodyOperationType.REMOVE, "endBound" : BoundingType.THROUGH_ALL, "depth" : 25.4 * mm, "offsetDistance" : 25.4 * mm});
        }
        {
            var Q0;
            Q0=qCreatedBy(makeId("Right.planeOp"),FACE);
            var sketch = newSketch(context, id + "F20", { "sketchPlane" : qUnion([Q0])});
            skCircle(sketch, "E51", {"center": v(0, -34.93) * mm, "radius": 3.18 * mm});
            skSolve(sketch);
        }
        {
            var Q0;
            Q0 = qSketchRegion(id + "F20", true);
            extrude(context, id + "F21", {"entities" : qUnion([Q0]), "operationType" : NewBodyOperationType.REMOVE, "oppositeDirection" : true, "depth" : 76.2 * mm, "offsetDistance" : 25.4 * mm});
        }
        {
            var Q0;
            Q0=makeQuery(id+"F1.opRevolve","SWEPT_FACE",FACE,{"disambiguationData":[OSD([sQuery(id+"F0.wireOp",EDGE,"E7")])]});
            var sketch = newSketch(context, id + "F22", { "sketchPlane" : qUnion([Q0])});
            skCircle(sketch, "E52", {"center": v(0, 0) * mm, "radius": 28.26 * mm});
            skCircle(sketch, "E53", {"center": v(0, 0) * mm, "radius": 29.85 * mm});
            skSolve(sketch);
        }
        {
            var Q0;
            Q0 = qSketchRegion(id + "F22", true);
            extrude(context, id + "F23", {"entities" : qUnion([Q0]), "operationType" : NewBodyOperationType.REMOVE, "oppositeDirection" : true, "depth" : 12.7 * mm, "offsetDistance" : 25.4 * mm});
        }
        {
            var Q0;
            Q0=qCreatedBy(makeId("Front.planeOp"),FACE);
            var sketch = newSketch(context, id + "F24", { "sketchPlane" : qUnion([Q0])});
            skLineSegment(sketch, "E54", {"start": v(0, 0) * mm, "end": v(0, -180.64) * mm});
            skSolve(sketch);
        }
    });
